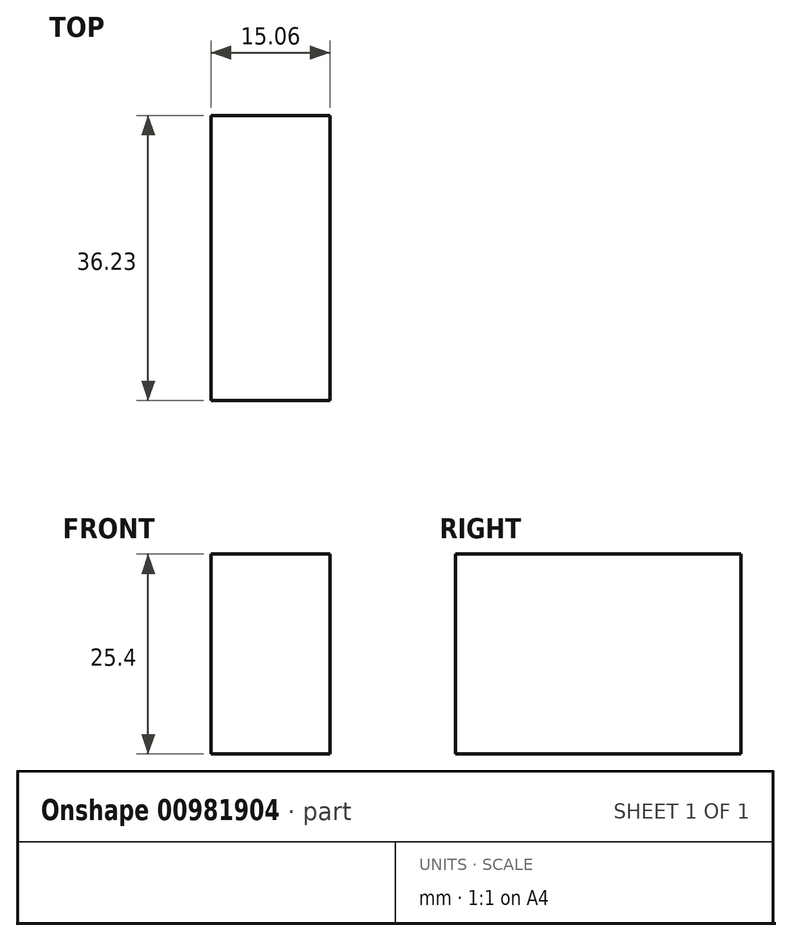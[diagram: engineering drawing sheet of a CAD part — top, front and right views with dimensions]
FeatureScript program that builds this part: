
annotation { "Feature Type Name" : "Feature", "Feature Type Description" : "" }
export const myFeature = defineFeature(function(context is Context, id is Id, definition is map)
    precondition{}
    {
        {
            var Q0;
            Q0=qCreatedBy(makeId("Top.planeOp"),FACE);
            var sketch = newSketch(context, id + "F0", { "sketchPlane" : qUnion([Q0])});
            skLineSegment(sketch, "E0.bottom", {"start": v(15.06, -36.23) * mm, "end": v(0, -36.23) * mm});
            skLineSegment(sketch, "E0.top", {"start": v(15.06, 0) * mm, "end": v(0, 0) * mm});
            skLineSegment(sketch, "E0.left", {"start": v(15.06, -36.23) * mm, "end": v(15.06, 0) * mm});
            skLineSegment(sketch, "E0.right", {"start": v(0, -36.23) * mm, "end": v(0, 0) * mm});
            skSolve(sketch);
        }
        {
            var Q0;
            Q0 = qSketchRegion(id + "F0", true);
            var Q1;
            Q1=makeQuery(id+"F0.imprint","IMPRINT",FACE,{"disambiguationData":[TD([[makeQuery(id+"F0.imprint","IMPRINT",EDGE,{"derivedFrom":sQuery(id+"F0.wireOp",EDGE,"E0.bottom")}),-1.0]])]});
            extrude(context, id + "F1", {"entities" : qUnion([Q0, Q1]), "depth" : 25.4 * mm, "offsetDistance" : 25.4 * mm});
        }
    });
